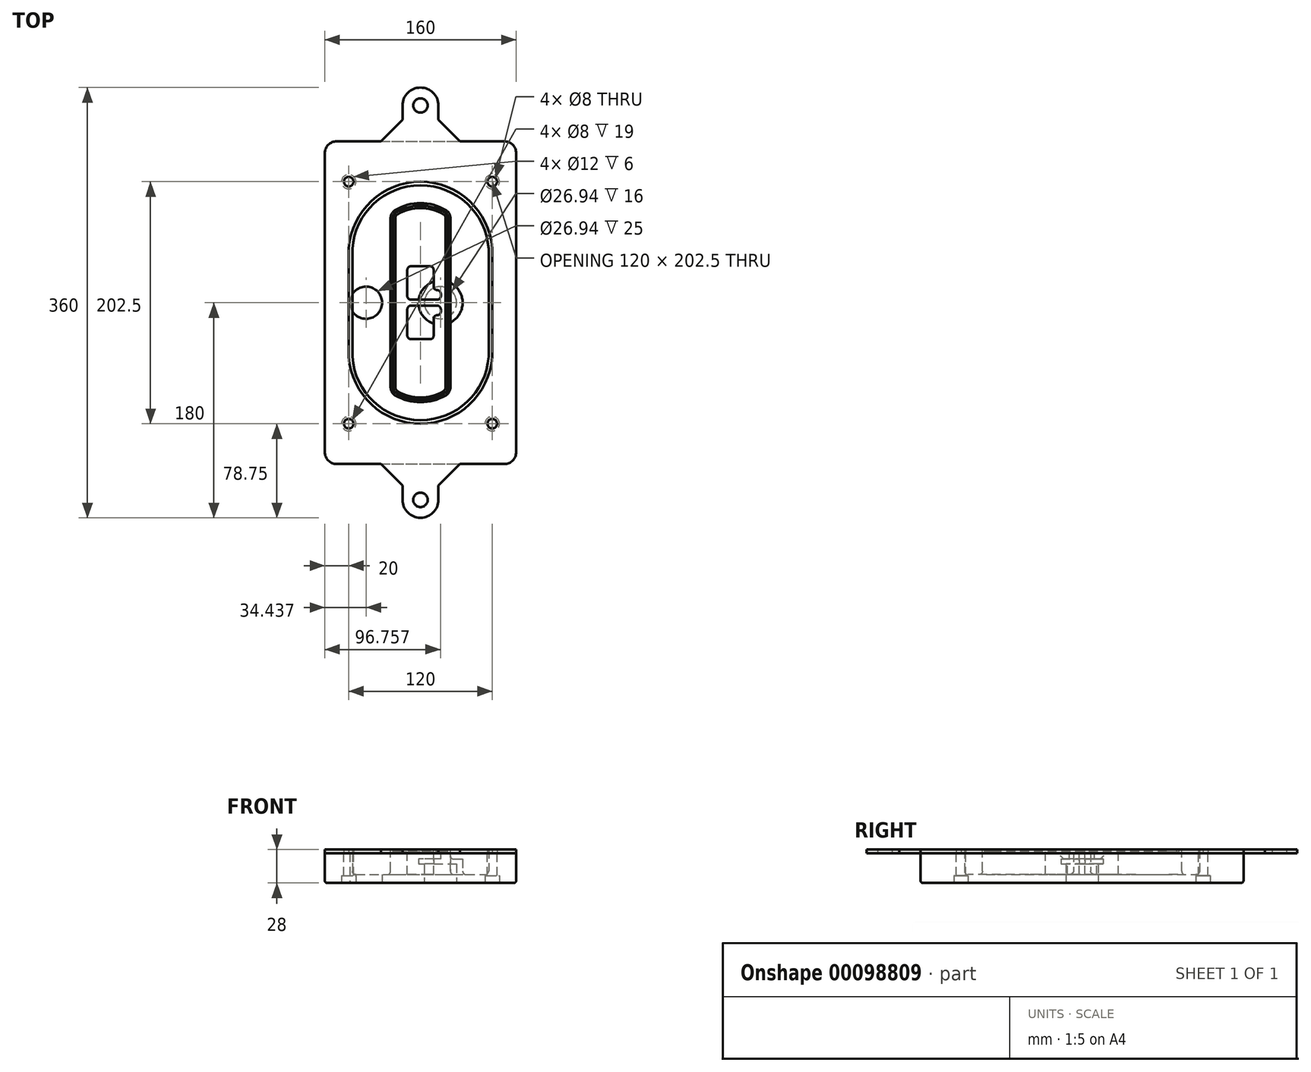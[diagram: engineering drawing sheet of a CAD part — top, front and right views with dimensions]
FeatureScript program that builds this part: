
annotation { "Feature Type Name" : "Feature", "Feature Type Description" : "" }
export const myFeature = defineFeature(function(context is Context, id is Id, definition is map)
    precondition{}
    {
        {
            var Q0;
            Q0=qCreatedBy(makeId("Top.planeOp"),FACE);
            var sketch = newSketch(context, id + "F0", { "sketchPlane" : qUnion([Q0])});
            skPoint(sketch, "E0.rect.middle", {"position": v(0, 0) * mm});
            skLineSegment(sketch, "E1.bottom", {"start": v(-70, -135) * mm, "end": v(70, -135) * mm});
            skLineSegment(sketch, "E1.top", {"start": v(-70, 135) * mm, "end": v(70, 135) * mm});
            skLineSegment(sketch, "E1.left", {"start": v(-80, -125) * mm, "end": v(-80, 125) * mm});
            skLineSegment(sketch, "E1.right", {"start": v(80, -125) * mm, "end": v(80, 125) * mm});
            skLineSegment(sketch, "E2", {"start": v(-80, 135) * mm, "end": v(80, -135) * mm, "construction": true});
            skLineSegment(sketch, "E3", {"start": v(80, 135) * mm, "end": v(-80, -135) * mm, "construction": true});
            skCircle(sketch, "E4", {"center": v(-60, 101.25) * mm, "radius": 4 * mm});
            skCircle(sketch, "E5", {"center": v(60, 101.25) * mm, "radius": 4 * mm});
            skCircle(sketch, "E6", {"center": v(60, -101.25) * mm, "radius": 4 * mm});
            skCircle(sketch, "E7", {"center": v(-60, -101.25) * mm, "radius": 4 * mm});
            skLineSegment(sketch, "E8", {"start": v(-60, 101.25) * mm, "end": v(60, 101.25) * mm, "construction": true});
            skLineSegment(sketch, "E9", {"start": v(60, 101.25) * mm, "end": v(60, -101.25) * mm, "construction": true});
            skLineSegment(sketch, "E10", {"start": v(60, -101.25) * mm, "end": v(-60, -101.25) * mm, "construction": true});
            skLineSegment(sketch, "E11", {"start": v(-60, -101.25) * mm, "end": v(-60, 101.25) * mm, "construction": true});
            skLineSegment(sketch, "E12", {"start": v(-60, 44.66) * mm, "end": v(-60, -44.66) * mm});
            skLineSegment(sketch, "E13", {"start": v(60, 44.66) * mm, "end": v(60, -44.66) * mm});
            skArc(sketch, "E14", {"start": v(59.98, 45.37) * mm, "mid": v(0, 101.25) * mm, "end": v(-59.98, 45.37) * mm});
            skArc(sketch, "E15", {"start": v(-59.98, -45.37) * mm, "mid": v(0, -101.25) * mm, "end": v(59.98, -45.37) * mm});
            skLineSegment(sketch, "E16", {"start": v(-60, 0) * mm, "end": v(60, 0) * mm, "construction": true});
            skPoint(sketch, "E17.visualSharp", {"position": v(-60, -45) * mm});
            skArc(sketch, "E17.filletArc", {"start": v(-60, -44.66) * mm, "mid": v(-60, -45.02) * mm, "end": v(-59.98, -45.37) * mm});
            skPoint(sketch, "E18.visualSharp", {"position": v(-60, 45) * mm});
            skArc(sketch, "E18.filletArc", {"start": v(-59.98, 45.37) * mm, "mid": v(-60, 45.02) * mm, "end": v(-60, 44.66) * mm});
            skPoint(sketch, "E19.visualSharp", {"position": v(60, 45) * mm});
            skArc(sketch, "E19.filletArc", {"start": v(60, 44.66) * mm, "mid": v(60, 45.02) * mm, "end": v(59.98, 45.37) * mm});
            skPoint(sketch, "E20.visualSharp", {"position": v(60, -45) * mm});
            skArc(sketch, "E20.filletArc", {"start": v(59.98, -45.37) * mm, "mid": v(60, -45.02) * mm, "end": v(60, -44.66) * mm});
            skPoint(sketch, "E21.visualSharp", {"position": v(-80, 135) * mm});
            skArc(sketch, "E21.filletArc", {"start": v(-70, 135) * mm, "mid": v(-77.07, 132.07) * mm, "end": v(-80, 125) * mm});
            skPoint(sketch, "E22.visualSharp", {"position": v(80, 135) * mm});
            skArc(sketch, "E22.filletArc", {"start": v(80, 125) * mm, "mid": v(77.07, 132.07) * mm, "end": v(70, 135) * mm});
            skPoint(sketch, "E23.visualSharp", {"position": v(80, -135) * mm});
            skArc(sketch, "E23.filletArc", {"start": v(70, -135) * mm, "mid": v(77.07, -132.07) * mm, "end": v(80, -125) * mm});
            skPoint(sketch, "E24.visualSharp", {"position": v(-80, -135) * mm});
            skArc(sketch, "E24.filletArc", {"start": v(-80, -125) * mm, "mid": v(-77.07, -132.07) * mm, "end": v(-70, -135) * mm});
            skArc(sketch, "E25.0", {"start": v(57, 44.66) * mm, "mid": v(57, 44.9) * mm, "end": v(56.98, 45.16) * mm});
            skLineSegment(sketch, "E25.1", {"start": v(57, 44.66) * mm, "end": v(57, -44.66) * mm});
            skArc(sketch, "E25.2", {"start": v(56.98, -45.16) * mm, "mid": v(57, -44.9) * mm, "end": v(57, -44.66) * mm});
            skArc(sketch, "E25.3", {"start": v(-56.98, -45.16) * mm, "mid": v(0, -98.25) * mm, "end": v(56.98, -45.16) * mm});
            skArc(sketch, "E25.4", {"start": v(-57, -44.66) * mm, "mid": v(-57, -44.9) * mm, "end": v(-56.98, -45.16) * mm});
            skArc(sketch, "E25.5", {"start": v(56.98, 45.16) * mm, "mid": v(0, 98.25) * mm, "end": v(-56.98, 45.16) * mm});
            skLineSegment(sketch, "E25.6", {"start": v(-57, 44.66) * mm, "end": v(-57, -44.66) * mm});
            skArc(sketch, "E25.7", {"start": v(-56.98, 45.16) * mm, "mid": v(-57, 44.9) * mm, "end": v(-57, 44.66) * mm});
            skArc(sketch, "E26.0", {"start": v(-63.97, 45.65) * mm, "mid": v(-64, 45.16) * mm, "end": v(-64, 44.66) * mm});
            skArc(sketch, "E26.1", {"start": v(63.97, 45.65) * mm, "mid": v(0, 105.25) * mm, "end": v(-63.97, 45.65) * mm});
            skArc(sketch, "E26.2", {"start": v(64, 44.66) * mm, "mid": v(64, 45.16) * mm, "end": v(63.97, 45.65) * mm});
            skLineSegment(sketch, "E26.3", {"start": v(64, 44.66) * mm, "end": v(64, -44.66) * mm});
            skArc(sketch, "E26.4", {"start": v(63.97, -45.65) * mm, "mid": v(64, -45.16) * mm, "end": v(64, -44.66) * mm});
            skLineSegment(sketch, "E26.5", {"start": v(-64, 44.66) * mm, "end": v(-64, -44.66) * mm});
            skArc(sketch, "E26.6", {"start": v(-63.97, -45.65) * mm, "mid": v(0, -105.25) * mm, "end": v(63.97, -45.65) * mm});
            skArc(sketch, "E26.7", {"start": v(-64, -44.66) * mm, "mid": v(-64, -45.16) * mm, "end": v(-63.97, -45.65) * mm});
            skSolve(sketch);
        }
        {
            var Q0;
            Q0=makeQuery(id+"F0.imprint","IMPRINT",FACE,{"disambiguationData":[TD([[makeQuery(id+"F0.imprint","IMPRINT",EDGE,{"derivedFrom":sQuery(id+"F0.wireOp",EDGE,"E1.bottom")}),1.0]])]});
            var Q1;
            Q1=makeQuery(id+"F0.imprint","IMPRINT",FACE,{"disambiguationData":[TD([[makeQuery(id+"F0.imprint","IMPRINT",EDGE,{"derivedFrom":sQuery(id+"F0.wireOp",EDGE,"E12")}),1.0]])]});
            var Q2;
            Q2=makeQuery(id+"F0.imprint","IMPRINT",FACE,{"disambiguationData":[TD([[makeQuery(id+"F0.imprint","IMPRINT",EDGE,{"derivedFrom":sQuery(id+"F0.wireOp",EDGE,"E25.0")}),1.0]])]});
            var Q3;
            Q3=makeQuery(id+"F0.imprint","IMPRINT",FACE,{"disambiguationData":[TD([[makeQuery(id+"F0.imprint","IMPRINT",EDGE,{"derivedFrom":sQuery(id+"F0.wireOp",EDGE,"E12")}),-1.0]])]});
            extrude(context, id + "F1", {"entities" : qUnion([Q0, Q1, Q2, Q3]), "oppositeDirection" : true, "depth" : 25 * mm});
        }
        {
            var Q0;
            Q0=makeQuery(id+"F0.imprint","IMPRINT",FACE,{"disambiguationData":[TD([[makeQuery(id+"F0.imprint","IMPRINT",EDGE,{"derivedFrom":sQuery(id+"F0.wireOp",EDGE,"E12")}),1.0]])]});
            extrude(context, id + "F2", {"entities" : qUnion([Q0]), "operationType" : NewBodyOperationType.ADD, "depth" : 3 * mm});
        }
        {
            var Q0;
            Q0=makeQuery(id+"F0.imprint","IMPRINT",FACE,{"disambiguationData":[TD([[makeQuery(id+"F0.imprint","IMPRINT",EDGE,{"derivedFrom":sQuery(id+"F0.wireOp",EDGE,"E25.0")}),1.0]])]});
            extrude(context, id + "F3", {"entities" : qUnion([Q0]), "operationType" : NewBodyOperationType.REMOVE, "oppositeDirection" : true, "depth" : 18 * mm});
        }
        {
            var Q0;
            Q0=makeQuery(id+"F2.opExtrude","CAP_FACE",FACE,{"disambiguationData":[OSD([sQuery(id+"F0.wireOp",EDGE,"E12"),sQuery(id+"F0.wireOp",EDGE,"E13"),sQuery(id+"F0.wireOp",EDGE,"E14"),sQuery(id+"F0.wireOp",EDGE,"E15"),sQuery(id+"F0.wireOp",EDGE,"E17.filletArc"),sQuery(id+"F0.wireOp",EDGE,"E18.filletArc"),sQuery(id+"F0.wireOp",EDGE,"E19.filletArc"),sQuery(id+"F0.wireOp",EDGE,"E20.filletArc"),sQuery(id+"F0.wireOp",EDGE,"E25.0"),sQuery(id+"F0.wireOp",EDGE,"E25.1"),sQuery(id+"F0.wireOp",EDGE,"E25.2"),sQuery(id+"F0.wireOp",EDGE,"E25.3"),sQuery(id+"F0.wireOp",EDGE,"E25.4"),sQuery(id+"F0.wireOp",EDGE,"E25.5"),sQuery(id+"F0.wireOp",EDGE,"E25.6"),sQuery(id+"F0.wireOp",EDGE,"E25.7")])],"isStart":false});
            var sketch = newSketch(context, id + "F4", { "sketchPlane" : qUnion([Q0])});
            skArc(sketch, "E27.0", {"start": v(-20.99, -77.65) * mm, "mid": v(0, -83.25) * mm, "end": v(20.99, -77.65) * mm});
            skArc(sketch, "E28.0", {"start": v(20.99, 77.65) * mm, "mid": v(0, 83.25) * mm, "end": v(-20.99, 77.65) * mm});
            skLineSegment(sketch, "E29", {"start": v(-25, 70.71) * mm, "end": v(-25, -70.71) * mm});
            skLineSegment(sketch, "E30", {"start": v(25, 70.71) * mm, "end": v(25, -70.71) * mm});
            skLineSegment(sketch, "E31", {"start": v(-25, 75.03) * mm, "end": v(25, 75.03) * mm, "construction": true});
            skLineSegment(sketch, "E32", {"start": v(-25, -75.03) * mm, "end": v(25, -75.03) * mm, "construction": true});
            skPoint(sketch, "E33.visualSharp", {"position": v(-25, 75.03) * mm});
            skArc(sketch, "E33.filletArc", {"start": v(-20.99, 77.65) * mm, "mid": v(-23.92, 74.72) * mm, "end": v(-25, 70.71) * mm});
            skPoint(sketch, "E34.visualSharp", {"position": v(25, 75.03) * mm});
            skArc(sketch, "E34.filletArc", {"start": v(25, 70.71) * mm, "mid": v(23.92, 74.72) * mm, "end": v(20.99, 77.65) * mm});
            skPoint(sketch, "E35.visualSharp", {"position": v(25, -75.03) * mm});
            skArc(sketch, "E35.filletArc", {"start": v(20.99, -77.65) * mm, "mid": v(23.92, -74.72) * mm, "end": v(25, -70.71) * mm});
            skPoint(sketch, "E36.visualSharp", {"position": v(-25, -75.03) * mm});
            skArc(sketch, "E36.filletArc", {"start": v(-25, -70.71) * mm, "mid": v(-23.92, -74.72) * mm, "end": v(-20.99, -77.65) * mm});
            skArc(sketch, "E37.0", {"start": v(56.98, 45.16) * mm, "mid": v(0, 98.25) * mm, "end": v(-56.98, 45.16) * mm});
            skArc(sketch, "E37.1", {"start": v(-56.98, 45.16) * mm, "mid": v(-57, 44.9) * mm, "end": v(-57, 44.66) * mm});
            skLineSegment(sketch, "E37.2", {"start": v(-57, 44.66) * mm, "end": v(-57, -44.66) * mm});
            skArc(sketch, "E37.3", {"start": v(-57, -44.66) * mm, "mid": v(-57, -44.9) * mm, "end": v(-56.98, -45.16) * mm});
            skArc(sketch, "E37.4", {"start": v(-56.98, -45.16) * mm, "mid": v(0, -98.25) * mm, "end": v(56.98, -45.16) * mm});
            skArc(sketch, "E37.5", {"start": v(56.98, -45.16) * mm, "mid": v(57, -44.9) * mm, "end": v(57, -44.66) * mm});
            skLineSegment(sketch, "E37.6", {"start": v(57, 44.66) * mm, "end": v(57, -44.66) * mm});
            skArc(sketch, "E37.7", {"start": v(57, 44.66) * mm, "mid": v(57, 44.9) * mm, "end": v(56.98, 45.16) * mm});
            skLineSegment(sketch, "E38.0", {"start": v(23, 70.71) * mm, "end": v(23, -70.71) * mm});
            skArc(sketch, "E38.1", {"start": v(19.99, -75.92) * mm, "mid": v(22.2, -73.72) * mm, "end": v(23, -70.71) * mm});
            skArc(sketch, "E38.2", {"start": v(-19.99, -75.92) * mm, "mid": v(0, -81.25) * mm, "end": v(19.99, -75.92) * mm});
            skArc(sketch, "E38.3", {"start": v(-23, -70.71) * mm, "mid": v(-22.2, -73.72) * mm, "end": v(-19.99, -75.92) * mm});
            skLineSegment(sketch, "E38.4", {"start": v(-23, 70.71) * mm, "end": v(-23, -70.71) * mm});
            skArc(sketch, "E38.5", {"start": v(23, 70.71) * mm, "mid": v(22.2, 73.72) * mm, "end": v(19.99, 75.92) * mm});
            skArc(sketch, "E38.6", {"start": v(-19.99, 75.92) * mm, "mid": v(-22.2, 73.72) * mm, "end": v(-23, 70.71) * mm});
            skArc(sketch, "E38.7", {"start": v(19.99, 75.92) * mm, "mid": v(0, 81.25) * mm, "end": v(-19.99, 75.92) * mm});
            skArc(sketch, "E39.0", {"start": v(21, 70.71) * mm, "mid": v(20.46, 72.72) * mm, "end": v(19, 74.18) * mm});
            skLineSegment(sketch, "E39.1", {"start": v(21, 70.71) * mm, "end": v(21, -70.71) * mm});
            skArc(sketch, "E39.2", {"start": v(19, -74.18) * mm, "mid": v(20.46, -72.72) * mm, "end": v(21, -70.71) * mm});
            skArc(sketch, "E39.3", {"start": v(-19, -74.18) * mm, "mid": v(0, -79.25) * mm, "end": v(19, -74.18) * mm});
            skArc(sketch, "E39.4", {"start": v(-21, -70.71) * mm, "mid": v(-20.46, -72.72) * mm, "end": v(-19, -74.18) * mm});
            skArc(sketch, "E39.5", {"start": v(19, 74.18) * mm, "mid": v(0, 79.25) * mm, "end": v(-19, 74.18) * mm});
            skLineSegment(sketch, "E39.6", {"start": v(-21, 70.71) * mm, "end": v(-21, -70.71) * mm});
            skArc(sketch, "E39.7", {"start": v(-19, 74.18) * mm, "mid": v(-20.46, 72.72) * mm, "end": v(-21, 70.71) * mm});
            skLineSegment(sketch, "E40", {"start": v(-25, 0) * mm, "end": v(25, 0) * mm, "construction": true});
            skLineSegment(sketch, "E41", {"start": v(-11, 5.5) * mm, "end": v(-11, 27.5) * mm});
            skLineSegment(sketch, "E42", {"start": v(-8, 30.5) * mm, "end": v(8, 30.5) * mm});
            skLineSegment(sketch, "E43", {"start": v(11, 27.5) * mm, "end": v(11, 13.5) * mm});
            skLineSegment(sketch, "E44", {"start": v(14, 10.5) * mm, "end": v(14, 10.5) * mm});
            skLineSegment(sketch, "E45", {"start": v(17, 7.5) * mm, "end": v(17, 5.5) * mm});
            skLineSegment(sketch, "E46", {"start": v(14, 2.5) * mm, "end": v(-8, 2.5) * mm});
            skPoint(sketch, "E47.visualSharp", {"position": v(-11, 30.5) * mm});
            skArc(sketch, "E47.filletArc", {"start": v(-8, 30.5) * mm, "mid": v(-10.12, 29.62) * mm, "end": v(-11, 27.5) * mm});
            skPoint(sketch, "E48.visualSharp", {"position": v(11, 30.5) * mm});
            skArc(sketch, "E48.filletArc", {"start": v(11, 27.5) * mm, "mid": v(10.12, 29.62) * mm, "end": v(8, 30.5) * mm});
            skPoint(sketch, "E49.visualSharp", {"position": v(11, 10.5) * mm});
            skArc(sketch, "E49.filletArc", {"start": v(11, 13.5) * mm, "mid": v(11.88, 11.38) * mm, "end": v(14, 10.5) * mm});
            skPoint(sketch, "E50.visualSharp", {"position": v(17, 10.5) * mm});
            skArc(sketch, "E50.filletArc", {"start": v(17, 7.5) * mm, "mid": v(16.12, 9.62) * mm, "end": v(14, 10.5) * mm});
            skPoint(sketch, "E51.visualSharp", {"position": v(17, 2.5) * mm});
            skArc(sketch, "E51.filletArc", {"start": v(14, 2.5) * mm, "mid": v(16.12, 3.38) * mm, "end": v(17, 5.5) * mm});
            skPoint(sketch, "E52.visualSharp", {"position": v(-11, 2.5) * mm});
            skArc(sketch, "E52.filletArc", {"start": v(-11, 5.5) * mm, "mid": v(-10.12, 3.38) * mm, "end": v(-8, 2.5) * mm});
            skLineSegment(sketch, "E53.0.MirrorCS", {"start": v(14, -2.5) * mm, "end": v(-8, -2.5) * mm});
            skArc(sketch, "E54.0.MirrorCS", {"start": v(-11, -5.5) * mm, "mid": v(-10.12, -3.38) * mm, "end": v(-8, -2.5) * mm});
            skLineSegment(sketch, "E55.0.MirrorCS", {"start": v(-11, -5.5) * mm, "end": v(-11, -27.5) * mm});
            skArc(sketch, "E56.0.MirrorCS", {"start": v(-8, -30.5) * mm, "mid": v(-10.12, -29.62) * mm, "end": v(-11, -27.5) * mm});
            skLineSegment(sketch, "E57.0.MirrorCS", {"start": v(-8, -30.5) * mm, "end": v(8, -30.5) * mm});
            skArc(sketch, "E58.0.MirrorCS", {"start": v(11, -27.5) * mm, "mid": v(10.12, -29.62) * mm, "end": v(8, -30.5) * mm});
            skLineSegment(sketch, "E59.0.MirrorCS", {"start": v(11, -27.5) * mm, "end": v(11, -13.5) * mm});
            skArc(sketch, "E60.0.MirrorCS", {"start": v(11, -13.5) * mm, "mid": v(11.88, -11.38) * mm, "end": v(14, -10.5) * mm});
            skArc(sketch, "E61.0.MirrorCS", {"start": v(17, -7.5) * mm, "mid": v(16.12, -9.62) * mm, "end": v(14, -10.5) * mm});
            skLineSegment(sketch, "E62.0.MirrorCS", {"start": v(17, -7.5) * mm, "end": v(17, -5.5) * mm});
            skArc(sketch, "E63.0.MirrorCS", {"start": v(14, -2.5) * mm, "mid": v(16.12, -3.38) * mm, "end": v(17, -5.5) * mm});
            skSolve(sketch);
        }
        {
            var Q0;
            Q0=makeQuery(id+"F4.imprint","IMPRINT",FACE,{"disambiguationData":[TD([[makeQuery(id+"F4.imprint","IMPRINT",EDGE,{"derivedFrom":sQuery(id+"F4.wireOp",EDGE,"E27.0")}),1.0]])]});
            var Q1;
            Q1=makeQuery(id+"F4.imprint","IMPRINT",FACE,{"disambiguationData":[TD([[makeQuery(id+"F4.imprint","IMPRINT",EDGE,{"derivedFrom":sQuery(id+"F4.wireOp",EDGE,"E38.0")}),-1.0]])]});
            var Q2;
            Q2=makeQuery(id+"F4.imprint","IMPRINT",FACE,{"disambiguationData":[TD([[makeQuery(id+"F4.imprint","IMPRINT",EDGE,{"derivedFrom":sQuery(id+"F4.wireOp",EDGE,"E39.0")}),1.0]])]});
            extrude(context, id + "F5", {"entities" : qUnion([Q0, Q1, Q2]), "operationType" : NewBodyOperationType.ADD, "endBound" : BoundingType.UP_TO_NEXT, "oppositeDirection" : true, "depth" : 25 * mm});
        }
        {
            var Q0;
            Q0=makeQuery(id+"F4.imprint","IMPRINT",FACE,{"disambiguationData":[TD([[makeQuery(id+"F4.imprint","IMPRINT",EDGE,{"derivedFrom":sQuery(id+"F4.wireOp",EDGE,"E38.0")}),-1.0]])]});
            extrude(context, id + "F6", {"entities" : qUnion([Q0]), "operationType" : NewBodyOperationType.REMOVE, "oppositeDirection" : true, "depth" : 2 * mm});
        }
        {
            var Q0;
            Q0=makeQuery(id+"F1.opExtrude","CAP_FACE",FACE,{"disambiguationData":[OSD([sQuery(id+"F0.wireOp",EDGE,"E1.bottom"),sQuery(id+"F0.wireOp",EDGE,"E1.top"),sQuery(id+"F0.wireOp",EDGE,"E1.left"),sQuery(id+"F0.wireOp",EDGE,"E1.right"),sQuery(id+"F0.wireOp",EDGE,"E4"),sQuery(id+"F0.wireOp",EDGE,"E5"),sQuery(id+"F0.wireOp",EDGE,"E6"),sQuery(id+"F0.wireOp",EDGE,"E7"),sQuery(id+"F0.wireOp",EDGE,"E21.filletArc"),sQuery(id+"F0.wireOp",EDGE,"E22.filletArc"),sQuery(id+"F0.wireOp",EDGE,"E23.filletArc"),sQuery(id+"F0.wireOp",EDGE,"E24.filletArc")])],"isStart":false});
            var sketch = newSketch(context, id + "F7", { "sketchPlane" : qUnion([Q0])});
            skCircle(sketch, "E64", {"center": v(16.76, 0) * mm, "radius": 13.47 * mm});
            skCircle(sketch, "E65", {"center": v(-45.56, 0) * mm, "radius": 13.47 * mm});
            skLineSegment(sketch, "E66", {"start": v(80, 0) * mm, "end": v(-80, 0) * mm});
            skCircle(sketch, "E67", {"center": v(16.76, 0) * mm, "radius": 18.47 * mm});
            skCircle(sketch, "E68", {"center": v(60, -101.25) * mm, "radius": 6 * mm});
            skCircle(sketch, "E69", {"center": v(-60, -101.25) * mm, "radius": 6 * mm});
            skCircle(sketch, "E70", {"center": v(-60, 101.25) * mm, "radius": 6 * mm});
            skCircle(sketch, "E71", {"center": v(60, 101.25) * mm, "radius": 6 * mm});
            skSolve(sketch);
        }
        {
            var Q0;
            {var subQ1=sQuery(id+"F7.wireOp",EDGE,"E66");var subQ4=sQuery(id+"F7.wireOp",EDGE,"E64");var subQ6=makeQuery(id+"F7.imprint","INTERSECT",VERTEX,{"disambiguationData":[OD(0.0)],"derivedFrom":[subQ4,subQ1]});Q0=makeQuery(id+"F7.imprint","IMPRINT",FACE,{"disambiguationData":[TD([[makeQuery(id+"F7.imprint","IMPRINT",EDGE,{"disambiguationData":[TD([[subQ6,-1.0]])],"derivedFrom":subQ4}),-1.0]])]});}
            var Q1;
            {var subQ0=sQuery(id+"F7.wireOp",EDGE,"E66");var subQ1=sQuery(id+"F7.wireOp",EDGE,"E64");var subQ3=makeQuery(id+"F7.imprint","INTERSECT",VERTEX,{"disambiguationData":[OD(0.0)],"derivedFrom":[subQ1,subQ0]});Q1=makeQuery(id+"F7.imprint","IMPRINT",FACE,{"disambiguationData":[TD([[makeQuery(id+"F7.imprint","IMPRINT",EDGE,{"disambiguationData":[TD([[subQ3,-1.0]])],"derivedFrom":subQ1}),1.0]])]});}
            var Q2;
            {var subQ0=sQuery(id+"F7.wireOp",EDGE,"E66");var subQ1=sQuery(id+"F7.wireOp",EDGE,"E64");var subQ3=makeQuery(id+"F7.imprint","INTERSECT",VERTEX,{"disambiguationData":[OD(0.0)],"derivedFrom":[subQ1,subQ0]});Q2=makeQuery(id+"F7.imprint","IMPRINT",FACE,{"disambiguationData":[TD([[makeQuery(id+"F7.imprint","IMPRINT",EDGE,{"disambiguationData":[TD([[subQ3,1.0]])],"derivedFrom":subQ1}),1.0]])]});}
            var Q3;
            {var subQ1=sQuery(id+"F7.wireOp",EDGE,"E66");var subQ4=sQuery(id+"F7.wireOp",EDGE,"E64");var subQ6=makeQuery(id+"F7.imprint","INTERSECT",VERTEX,{"disambiguationData":[OD(0.0)],"derivedFrom":[subQ4,subQ1]});Q3=makeQuery(id+"F7.imprint","IMPRINT",FACE,{"disambiguationData":[TD([[makeQuery(id+"F7.imprint","IMPRINT",EDGE,{"disambiguationData":[TD([[subQ6,1.0]])],"derivedFrom":subQ4}),-1.0]])]});}
            extrude(context, id + "F8", {"entities" : qUnion([Q0, Q1, Q2, Q3]), "operationType" : NewBodyOperationType.ADD, "oppositeDirection" : true, "depth" : 20 * mm});
        }
        {
            var Q0;
            {var subQ0=sQuery(id+"F7.wireOp",EDGE,"E66");var subQ1=sQuery(id+"F7.wireOp",EDGE,"E64");var subQ3=makeQuery(id+"F7.imprint","INTERSECT",VERTEX,{"disambiguationData":[OD(0.0)],"derivedFrom":[subQ1,subQ0]});Q0=makeQuery(id+"F7.imprint","IMPRINT",FACE,{"disambiguationData":[TD([[makeQuery(id+"F7.imprint","IMPRINT",EDGE,{"disambiguationData":[TD([[subQ3,-1.0]])],"derivedFrom":subQ1}),1.0]])]});}
            var Q1;
            {var subQ0=sQuery(id+"F7.wireOp",EDGE,"E66");var subQ1=sQuery(id+"F7.wireOp",EDGE,"E64");var subQ3=makeQuery(id+"F7.imprint","INTERSECT",VERTEX,{"disambiguationData":[OD(0.0)],"derivedFrom":[subQ1,subQ0]});Q1=makeQuery(id+"F7.imprint","IMPRINT",FACE,{"disambiguationData":[TD([[makeQuery(id+"F7.imprint","IMPRINT",EDGE,{"disambiguationData":[TD([[subQ3,1.0]])],"derivedFrom":subQ1}),1.0]])]});}
            extrude(context, id + "F9", {"entities" : qUnion([Q0, Q1]), "operationType" : NewBodyOperationType.REMOVE, "oppositeDirection" : true, "depth" : 16 * mm});
        }
        {
            var Q0;
            {var subQ0=sQuery(id+"F7.wireOp",EDGE,"E66");var subQ1=sQuery(id+"F7.wireOp",EDGE,"E65");var subQ3=makeQuery(id+"F7.imprint","INTERSECT",VERTEX,{"disambiguationData":[OD(0.0)],"derivedFrom":[subQ1,subQ0]});Q0=makeQuery(id+"F7.imprint","IMPRINT",FACE,{"disambiguationData":[TD([[makeQuery(id+"F7.imprint","IMPRINT",EDGE,{"disambiguationData":[TD([[subQ3,-1.0]])],"derivedFrom":subQ1}),1.0]])]});}
            var Q1;
            {var subQ0=sQuery(id+"F7.wireOp",EDGE,"E66");var subQ1=sQuery(id+"F7.wireOp",EDGE,"E65");var subQ3=makeQuery(id+"F7.imprint","INTERSECT",VERTEX,{"disambiguationData":[OD(0.0)],"derivedFrom":[subQ1,subQ0]});Q1=makeQuery(id+"F7.imprint","IMPRINT",FACE,{"disambiguationData":[TD([[makeQuery(id+"F7.imprint","IMPRINT",EDGE,{"disambiguationData":[TD([[subQ3,1.0]])],"derivedFrom":subQ1}),1.0]])]});}
            extrude(context, id + "F10", {"entities" : qUnion([Q0, Q1]), "operationType" : NewBodyOperationType.REMOVE, "oppositeDirection" : true, "depth" : 25 * mm});
        }
        {
            var Q0;
            Q0=makeQuery(id+"F7.imprint","IMPRINT",FACE,{"disambiguationData":[TD([[makeQuery(id+"F7.imprint","IMPRINT",EDGE,{"derivedFrom":sQuery(id+"F7.wireOp",EDGE,"E68")}),1.0]])]});
            var Q1;
            Q1=makeQuery(id+"F7.imprint","IMPRINT",FACE,{"disambiguationData":[TD([[makeQuery(id+"F7.imprint","IMPRINT",EDGE,{"derivedFrom":makeQuery(id+"F1.opExtrude","CAP_EDGE",EDGE,{"disambiguationData":[OSD([sQuery(id+"F0.wireOp",EDGE,"E5")])],"isStart":false})}),-1.0]])]});
            var Q2;
            Q2=makeQuery(id+"F7.imprint","IMPRINT",FACE,{"disambiguationData":[TD([[makeQuery(id+"F7.imprint","IMPRINT",EDGE,{"derivedFrom":sQuery(id+"F7.wireOp",EDGE,"E69")}),1.0]])]});
            var Q3;
            Q3=makeQuery(id+"F7.imprint","IMPRINT",FACE,{"disambiguationData":[TD([[makeQuery(id+"F7.imprint","IMPRINT",EDGE,{"derivedFrom":makeQuery(id+"F1.opExtrude","CAP_EDGE",EDGE,{"disambiguationData":[OSD([sQuery(id+"F0.wireOp",EDGE,"E4")])],"isStart":false})}),-1.0]])]});
            var Q4;
            Q4=makeQuery(id+"F7.imprint","IMPRINT",FACE,{"disambiguationData":[TD([[makeQuery(id+"F7.imprint","IMPRINT",EDGE,{"derivedFrom":sQuery(id+"F7.wireOp",EDGE,"E70")}),1.0]])]});
            var Q5;
            Q5=makeQuery(id+"F7.imprint","IMPRINT",FACE,{"disambiguationData":[TD([[makeQuery(id+"F7.imprint","IMPRINT",EDGE,{"derivedFrom":makeQuery(id+"F1.opExtrude","CAP_EDGE",EDGE,{"disambiguationData":[OSD([sQuery(id+"F0.wireOp",EDGE,"E7")])],"isStart":false})}),-1.0]])]});
            var Q6;
            Q6=makeQuery(id+"F7.imprint","IMPRINT",FACE,{"disambiguationData":[TD([[makeQuery(id+"F7.imprint","IMPRINT",EDGE,{"derivedFrom":sQuery(id+"F7.wireOp",EDGE,"E71")}),1.0]])]});
            var Q7;
            Q7=makeQuery(id+"F7.imprint","IMPRINT",FACE,{"disambiguationData":[TD([[makeQuery(id+"F7.imprint","IMPRINT",EDGE,{"derivedFrom":makeQuery(id+"F1.opExtrude","CAP_EDGE",EDGE,{"disambiguationData":[OSD([sQuery(id+"F0.wireOp",EDGE,"E6")])],"isStart":false})}),-1.0]])]});
            extrude(context, id + "F11", {"entities" : qUnion([Q0, Q1, Q2, Q3, Q4, Q5, Q6, Q7]), "operationType" : NewBodyOperationType.REMOVE, "oppositeDirection" : true, "depth" : 6 * mm});
        }
        {
            var Q0;
            Q0=makeQuery(id+"F9.boolean.opBoolean","COPY",FACE,{"derivedFrom":makeQuery(id+"F9.opExtrude","CAP_FACE",FACE,{"disambiguationData":[OSD([sQuery(id+"F7.wireOp",EDGE,"E64")])],"isStart":false})});
            var sketch = newSketch(context, id + "F12", { "sketchPlane" : qUnion([Q0])});
            skArc(sketch, "E72.0", {"start": v(11, 17.55) * mm, "mid": v(2.57, 11.82) * mm, "end": v(-1.54, 2.5) * mm});
            skArc(sketch, "E72.1", {"start": v(-1.54, -2.5) * mm, "mid": v(2.57, -11.82) * mm, "end": v(11, -17.55) * mm});
            skLineSegment(sketch, "E73", {"start": v(-1.54, -2.5) * mm, "end": v(14, -2.5) * mm});
            skLineSegment(sketch, "E74.0", {"start": v(14, 2.5) * mm, "end": v(-1.54, 2.5) * mm});
            skArc(sketch, "E74.1", {"start": v(14, 2.5) * mm, "mid": v(16.12, 3.38) * mm, "end": v(17, 5.5) * mm});
            skLineSegment(sketch, "E74.2", {"start": v(17, 7.5) * mm, "end": v(17, 5.5) * mm});
            skArc(sketch, "E74.3", {"start": v(17, 7.5) * mm, "mid": v(16.12, 9.62) * mm, "end": v(14, 10.5) * mm});
            skArc(sketch, "E74.4", {"start": v(11, 13.5) * mm, "mid": v(11.88, 11.38) * mm, "end": v(14, 10.5) * mm});
            skLineSegment(sketch, "E74.5", {"start": v(11, 17.55) * mm, "end": v(11, 13.5) * mm});
            skLineSegment(sketch, "E74.7", {"start": v(14, -2.5) * mm, "end": v(-1.54, -2.5) * mm});
            skArc(sketch, "E74.8", {"start": v(14, -2.5) * mm, "mid": v(16.12, -3.38) * mm, "end": v(17, -5.5) * mm});
            skLineSegment(sketch, "E74.9", {"start": v(17, -7.5) * mm, "end": v(17, -5.5) * mm});
            skArc(sketch, "E74.10", {"start": v(17, -7.5) * mm, "mid": v(16.12, -9.62) * mm, "end": v(14, -10.5) * mm});
            skArc(sketch, "E74.11", {"start": v(11, -13.5) * mm, "mid": v(11.88, -11.38) * mm, "end": v(14, -10.5) * mm});
            skLineSegment(sketch, "E74.12", {"start": v(11, -17.55) * mm, "end": v(11, -13.5) * mm});
            skPoint(sketch, "E75.orphan", {"position": v(11, -27.5) * mm});
            skPoint(sketch, "E76.orphan", {"position": v(-8, -2.5) * mm});
            skPoint(sketch, "E77.orphan", {"position": v(-8, 2.5) * mm});
            skPoint(sketch, "E78.orphan", {"position": v(11, 27.5) * mm});
            skSolve(sketch);
        }
        {
            var Q0;
            {var subQ7=sQuery(id+"F12.wireOp",EDGE,"E72.0");var subQ14=sQuery(id+"F12.wireOp",EDGE,"E72.1");var subQ16=sQuery(id+"F12.wireOp",EDGE,"E74.1");var subQ18=sQuery(id+"F12.wireOp",EDGE,"E74.8");Q0=qUnion([makeQuery(id+"F12.imprint","IMPRINT",FACE,{"disambiguationData":[TD([[makeQuery(id+"F12.imprint","IMPRINT",EDGE,{"derivedFrom":subQ7}),1.0]])]}),makeQuery(id+"F12.imprint","IMPRINT",FACE,{"disambiguationData":[TD([[makeQuery(id+"F12.imprint","IMPRINT",EDGE,{"derivedFrom":subQ14}),1.0]])]}),makeQuery(id+"F12.imprint","IMPRINT",FACE,{"disambiguationData":[TD([[makeQuery(id+"F12.imprint","IMPRINT",EDGE,{"derivedFrom":subQ16}),1.0]])]}),makeQuery(id+"F12.imprint","IMPRINT",FACE,{"disambiguationData":[TD([[makeQuery(id+"F12.imprint","IMPRINT",EDGE,{"derivedFrom":subQ18}),-1.0]])]})]);}
            var Q1;
            Q1=makeQuery(id+"F5.boolean.opBoolean","SPLIT",FACE,{"disambiguationData":[TD([makeQuery(id+"F5.opExtrude","SWEPT_FACE",FACE,{"disambiguationData":[OSD([sQuery(id+"F4.wireOp",EDGE,"E41")])]})])],"derivedFrom":makeQuery(id+"F3.boolean.opBoolean","COPY",FACE,{"derivedFrom":makeQuery(id+"F3.opExtrude","CAP_FACE",FACE,{"disambiguationData":[OSD([sQuery(id+"F0.wireOp",EDGE,"E25.0"),sQuery(id+"F0.wireOp",EDGE,"E25.1"),sQuery(id+"F0.wireOp",EDGE,"E25.2"),sQuery(id+"F0.wireOp",EDGE,"E25.3"),sQuery(id+"F0.wireOp",EDGE,"E25.4"),sQuery(id+"F0.wireOp",EDGE,"E25.5"),sQuery(id+"F0.wireOp",EDGE,"E25.6"),sQuery(id+"F0.wireOp",EDGE,"E25.7")])],"isStart":false})})});
            extrude(context, id + "F13", {"entities" : qUnion([Q0]), "operationType" : NewBodyOperationType.REMOVE, "endBound" : BoundingType.UP_TO_SURFACE, "endBoundEntityFace" : qUnion([Q1]), "depth" : 25 * mm});
        }
        {
            var Q0;
            Q0=makeQuery(id+"F3.boolean.opBoolean","COPY",EDGE,{"derivedFrom":makeQuery(id+"F3.opExtrude","CAP_EDGE",EDGE,{"disambiguationData":[OSD([sQuery(id+"F0.wireOp",EDGE,"E25.6")])],"isStart":false})});
            var Q1;
            Q1=makeQuery(id+"F8.boolean.opBoolean","INTERSECT",EDGE,{"derivedFrom":[makeQuery(id+"F5.opExtrude","SWEPT_FACE",FACE,{"disambiguationData":[OSD([sQuery(id+"F4.wireOp",EDGE,"E30")])]}),makeQuery(id+"F8.opExtrude","CAP_FACE",FACE,{"disambiguationData":[OSD([sQuery(id+"F7.wireOp",EDGE,"E67")])],"isStart":false})]});
            var Q2;
            Q2=makeQuery(id+"F8.boolean.opBoolean","INTERSECT",EDGE,{"disambiguationData":[OD(1.0)],"derivedFrom":[makeQuery(id+"F5.opExtrude","SWEPT_FACE",FACE,{"disambiguationData":[OSD([sQuery(id+"F4.wireOp",EDGE,"E30")])]}),makeQuery(id+"F8.opExtrude","SWEPT_FACE",FACE,{"disambiguationData":[OSD([sQuery(id+"F7.wireOp",EDGE,"E67")])]})]});
            var Q3;
            {var subQ0=sQuery(id+"F4.wireOp",EDGE,"E30");Q3=makeQuery(id+"F8.boolean.opBoolean","SPLIT",EDGE,{"disambiguationData":[TD([makeQuery(id+"F5.opExtrude","SWEPT_FACE",FACE,{"disambiguationData":[OSD([sQuery(id+"F4.wireOp",EDGE,"E35.filletArc")])]})])],"derivedFrom":makeQuery(id+"F5.opExtrude","CAP_EDGE",EDGE,{"disambiguationData":[OSD([subQ0])],"isStart":false})});}
            var Q4;
            {var subQ0=sQuery(id+"F0.wireOp",EDGE,"E25.7");var subQ1=sQuery(id+"F0.wireOp",EDGE,"E25.1");var subQ2=sQuery(id+"F0.wireOp",EDGE,"E25.6");var subQ3=sQuery(id+"F0.wireOp",EDGE,"E25.5");var subQ4=sQuery(id+"F0.wireOp",EDGE,"E25.4");var subQ5=sQuery(id+"F0.wireOp",EDGE,"E25.0");var subQ6=sQuery(id+"F0.wireOp",EDGE,"E25.2");var subQ7=sQuery(id+"F0.wireOp",EDGE,"E25.3");Q4=makeQuery(id+"F8.boolean.opBoolean","INTERSECT",EDGE,{"derivedFrom":[makeQuery(id+"F5.boolean.opBoolean","SPLIT",FACE,{"disambiguationData":[TD([makeQuery(id+"F2.opExtrude","SWEPT_FACE",FACE,{"disambiguationData":[OSD([subQ5])]})])],"derivedFrom":makeQuery(id+"F3.boolean.opBoolean","COPY",FACE,{"derivedFrom":makeQuery(id+"F3.opExtrude","CAP_FACE",FACE,{"disambiguationData":[OSD([subQ5,subQ1,subQ6,subQ7,subQ4,subQ3,subQ2,subQ0])],"isStart":false})})}),makeQuery(id+"F8.opExtrude","SWEPT_FACE",FACE,{"disambiguationData":[OSD([sQuery(id+"F7.wireOp",EDGE,"E67")])]})]});}
            var Q5;
            Q5=makeQuery(id+"F8.boolean.opBoolean","INTERSECT",EDGE,{"disambiguationData":[OD(0.0)],"derivedFrom":[makeQuery(id+"F5.opExtrude","SWEPT_FACE",FACE,{"disambiguationData":[OSD([sQuery(id+"F4.wireOp",EDGE,"E30")])]}),makeQuery(id+"F8.opExtrude","SWEPT_FACE",FACE,{"disambiguationData":[OSD([sQuery(id+"F7.wireOp",EDGE,"E67")])]})]});
            fillet(context, id + "F14", {"entities" : qUnion([Q0, Q1, Q2, Q3, Q4, Q5]), "radius" : 3 * mm, "tangentPropagation" : true, "allowEdgeOverflow" : false});
        }
        {
            var Q0;
            Q0=makeQuery(id+"F1.opExtrude","CAP_EDGE",EDGE,{"disambiguationData":[OSD([sQuery(id+"F0.wireOp",EDGE,"E1.bottom")])],"isStart":false});
            fillet(context, id + "F15", {"entities" : qUnion([Q0]), "radius" : 2 * mm, "tangentPropagation" : true, "allowEdgeOverflow" : false});
        }
        {
            var Q0;
            {var subQ0=sQuery(id+"F0.wireOp",EDGE,"E22.filletArc");var subQ1=sQuery(id+"F0.wireOp",EDGE,"E7");var subQ2=sQuery(id+"F0.wireOp",EDGE,"E6");var subQ3=sQuery(id+"F0.wireOp",EDGE,"E5");var subQ4=sQuery(id+"F0.wireOp",EDGE,"E4");var subQ5=sQuery(id+"F0.wireOp",EDGE,"E1.bottom");var subQ6=sQuery(id+"F0.wireOp",EDGE,"E21.filletArc");var subQ7=sQuery(id+"F0.wireOp",EDGE,"E1.top");var subQ8=sQuery(id+"F0.wireOp",EDGE,"E1.left");var subQ9=sQuery(id+"F0.wireOp",EDGE,"E1.right");var subQ10=sQuery(id+"F0.wireOp",EDGE,"E23.filletArc");var subQ11=sQuery(id+"F0.wireOp",EDGE,"E24.filletArc");Q0=makeQuery(id+"F2.boolean.opBoolean","SPLIT",FACE,{"disambiguationData":[TD([makeQuery(id+"F1.opExtrude","SWEPT_FACE",FACE,{"disambiguationData":[OSD([subQ5])]})])],"derivedFrom":makeQuery(id+"F1.opExtrude","CAP_FACE",FACE,{"disambiguationData":[OSD([subQ5,subQ7,subQ8,subQ9,subQ4,subQ3,subQ2,subQ1,subQ6,subQ0,subQ10,subQ11])],"isStart":true})});}
            var sketch = newSketch(context, id + "F16", { "sketchPlane" : qUnion([Q0])});
            skLineSegment(sketch, "E79", {"start": v(0, 135) * mm, "end": v(0, 165) * mm, "construction": true});
            skCircle(sketch, "E80", {"center": v(0, 165) * mm, "radius": 6 * mm});
            skArc(sketch, "E81", {"start": v(15, 165) * mm, "mid": v(0, 180) * mm, "end": v(-15, 165) * mm});
            skLineSegment(sketch, "E82", {"start": v(-15, 165) * mm, "end": v(-15, 153) * mm});
            skLineSegment(sketch, "E83", {"start": v(-15, 153) * mm, "end": v(-33, 135) * mm});
            skLineSegment(sketch, "E84", {"start": v(15, 165) * mm, "end": v(15, 153) * mm});
            skLineSegment(sketch, "E85", {"start": v(15, 153) * mm, "end": v(33, 135) * mm});
            skLineSegment(sketch, "E86", {"start": v(-93.26, 0) * mm, "end": v(93.74, 0) * mm, "construction": true});
            skPoint(sketch, "E86.startSnap0", {"position": v(-60, 0) * mm});
            skPoint(sketch, "E86.endSnap0", {"position": v(80, 0) * mm});
            skArc(sketch, "E87.2", {"start": v(-70, 135) * mm, "mid": v(-77.07, 132.07) * mm, "end": v(-80, 125) * mm});
            skLineSegment(sketch, "E87.3", {"start": v(-80, -125) * mm, "end": v(-80, 125) * mm});
            skArc(sketch, "E87.4", {"start": v(-80, -125) * mm, "mid": v(-77.07, -132.07) * mm, "end": v(-70, -135) * mm});
            skLineSegment(sketch, "E87.5", {"start": v(-70, -135) * mm, "end": v(70, -135) * mm});
            skArc(sketch, "E87.6", {"start": v(70, -135) * mm, "mid": v(77.07, -132.07) * mm, "end": v(80, -125) * mm});
            skLineSegment(sketch, "E87.7", {"start": v(80, -125) * mm, "end": v(80, 125) * mm});
            skPoint(sketch, "E87.8", {"position": v(80, 125) * mm});
            skArc(sketch, "E87.9", {"start": v(80, 125) * mm, "mid": v(77.07, 132.07) * mm, "end": v(70, 135) * mm});
            skLineSegment(sketch, "E87.10", {"start": v(-70, 135) * mm, "end": v(70, 135) * mm});
            skArc(sketch, "E87.11", {"start": v(59.98, 45.37) * mm, "mid": v(0, 101.25) * mm, "end": v(-59.98, 45.37) * mm});
            skArc(sketch, "E87.12", {"start": v(-59.98, 45.37) * mm, "mid": v(-60, 45.02) * mm, "end": v(-60, 44.66) * mm});
            skLineSegment(sketch, "E87.13", {"start": v(-60, 44.66) * mm, "end": v(-60, -44.66) * mm});
            skArc(sketch, "E87.14", {"start": v(-60, -44.66) * mm, "mid": v(-60, -45.02) * mm, "end": v(-59.98, -45.37) * mm});
            skArc(sketch, "E87.15", {"start": v(-59.98, -45.37) * mm, "mid": v(0, -101.25) * mm, "end": v(59.98, -45.37) * mm});
            skArc(sketch, "E87.16", {"start": v(59.98, -45.37) * mm, "mid": v(60, -45.02) * mm, "end": v(60, -44.66) * mm});
            skLineSegment(sketch, "E87.17", {"start": v(60, 44.66) * mm, "end": v(60, -44.66) * mm});
            skArc(sketch, "E87.18", {"start": v(60, 44.66) * mm, "mid": v(60, 45.02) * mm, "end": v(59.98, 45.37) * mm});
            skCircle(sketch, "E87.19", {"center": v(60, 101.25) * mm, "radius": 4 * mm});
            skCircle(sketch, "E87.20", {"center": v(-60, 101.25) * mm, "radius": 4 * mm});
            skCircle(sketch, "E87.21", {"center": v(-60, -101.25) * mm, "radius": 4 * mm});
            skCircle(sketch, "E87.22", {"center": v(60, -101.25) * mm, "radius": 4 * mm});
            skLineSegment(sketch, "E88.MirrorCS", {"start": v(-15, -153) * mm, "end": v(-33, -135) * mm});
            skLineSegment(sketch, "E89.MirrorCS", {"start": v(-15, -165) * mm, "end": v(-15, -153) * mm});
            skArc(sketch, "E90.MirrorCS", {"start": v(15, -165) * mm, "mid": v(0, -180) * mm, "end": v(-15, -165) * mm});
            skLineSegment(sketch, "E91.MirrorCS", {"start": v(15, -165) * mm, "end": v(15, -153) * mm});
            skLineSegment(sketch, "E92.MirrorCS", {"start": v(15, -153) * mm, "end": v(33, -135) * mm});
            skLineSegment(sketch, "E93.MirrorCS", {"start": v(0, -135) * mm, "end": v(0, -165) * mm, "construction": true});
            skCircle(sketch, "E94.MirrorC", {"center": v(0, -165) * mm, "radius": 6 * mm});
            skSolve(sketch);
        }
        {
            var Q0;
            {var subQ0=sQuery(id+"F16.wireOp",EDGE,"E88.MirrorCS");Q0=makeQuery(id+"F16.imprint","IMPRINT",FACE,{"disambiguationData":[TD([[makeQuery(id+"F16.imprint","IMPRINT",EDGE,{"derivedFrom":subQ0}),-1.0]])]});}
            var Q1;
            Q1=makeQuery(id+"F16.imprint","IMPRINT",FACE,{"disambiguationData":[TD([[makeQuery(id+"F16.imprint","IMPRINT",EDGE,{"derivedFrom":sQuery(id+"F16.wireOp",EDGE,"E80")}),-1.0]])]});
            var Q2;
            {var subQ7=sQuery(id+"F16.wireOp",EDGE,"E87.2");Q2=makeQuery(id+"F16.imprint","IMPRINT",FACE,{"disambiguationData":[TD([[makeQuery(id+"F16.imprint","IMPRINT",EDGE,{"derivedFrom":subQ7}),1.0]])]});}
            var Q3;
            {var subQ0=sQuery(id+"F4.wireOp",EDGE,"E36.filletArc");var subQ1=sQuery(id+"F4.wireOp",EDGE,"E35.filletArc");var subQ2=sQuery(id+"F4.wireOp",EDGE,"E34.filletArc");var subQ3=sQuery(id+"F4.wireOp",EDGE,"E33.filletArc");var subQ4=sQuery(id+"F4.wireOp",EDGE,"E27.0");var subQ5=sQuery(id+"F4.wireOp",EDGE,"E30");var subQ6=sQuery(id+"F4.wireOp",EDGE,"E28.0");var subQ7=sQuery(id+"F4.wireOp",EDGE,"E29");Q3=makeQuery(id+"F6.boolean.opBoolean","SPLIT",FACE,{"disambiguationData":[TD([makeQuery(id+"F5.opExtrude","SWEPT_FACE",FACE,{"disambiguationData":[OSD([subQ4])]})])],"derivedFrom":makeQuery(id+"F5.opExtrude","CAP_FACE",FACE,{"disambiguationData":[OSD([subQ4,subQ6,subQ7,subQ5,subQ3,subQ2,subQ1,subQ0,sQuery(id+"F4.wireOp",EDGE,"E41"),sQuery(id+"F4.wireOp",EDGE,"E42"),sQuery(id+"F4.wireOp",EDGE,"E43"),sQuery(id+"F4.wireOp",EDGE,"E45"),sQuery(id+"F4.wireOp",EDGE,"E46"),sQuery(id+"F4.wireOp",EDGE,"E47.filletArc"),sQuery(id+"F4.wireOp",EDGE,"E48.filletArc"),sQuery(id+"F4.wireOp",EDGE,"E49.filletArc"),sQuery(id+"F4.wireOp",EDGE,"E50.filletArc"),sQuery(id+"F4.wireOp",EDGE,"E51.filletArc"),sQuery(id+"F4.wireOp",EDGE,"E52.filletArc"),sQuery(id+"F4.wireOp",EDGE,"E53.0.MirrorCS"),sQuery(id+"F4.wireOp",EDGE,"E54.0.MirrorCS"),sQuery(id+"F4.wireOp",EDGE,"E55.0.MirrorCS"),sQuery(id+"F4.wireOp",EDGE,"E56.0.MirrorCS"),sQuery(id+"F4.wireOp",EDGE,"E57.0.MirrorCS"),sQuery(id+"F4.wireOp",EDGE,"E58.0.MirrorCS"),sQuery(id+"F4.wireOp",EDGE,"E59.0.MirrorCS"),sQuery(id+"F4.wireOp",EDGE,"E60.0.MirrorCS"),sQuery(id+"F4.wireOp",EDGE,"E61.0.MirrorCS"),sQuery(id+"F4.wireOp",EDGE,"E62.0.MirrorCS"),sQuery(id+"F4.wireOp",EDGE,"E63.0.MirrorCS")])],"isStart":true})});}
            extrude(context, id + "F17", {"entities" : qUnion([Q0, Q1, Q2]), "endBound" : BoundingType.UP_TO_SURFACE, "endBoundEntityFace" : qUnion([Q3]), "depth" : 25 * mm});
        }
    });
